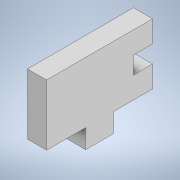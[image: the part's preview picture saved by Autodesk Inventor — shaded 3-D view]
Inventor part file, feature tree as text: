
AUTODESK INVENTOR PART (.ipt)
format: ipt  version: 2020 (Build 240168000, 168)  size: 114,688 bytes
history: native  units: mm
features: extrude x3, sketch x3
ambient origin geometry x8: Origin, YZ Plane, XZ Plane, XY Plane, X Axis, Y Axis, Z Axis, Center Point
bodies: Solide1 (feature_tree)
feature tree (6):
  extrude  "Extrusion1"  Depth=22.0mm
  extrude  "Extrusion2"  Depth=122.0mm
  extrude  "Extrusion3"  Depth=70.0mm TaperAngle=0.0deg
  sketch  "Esquisse1"
  sketch  "Esquisse2"
  sketch  "Esquisse3"
